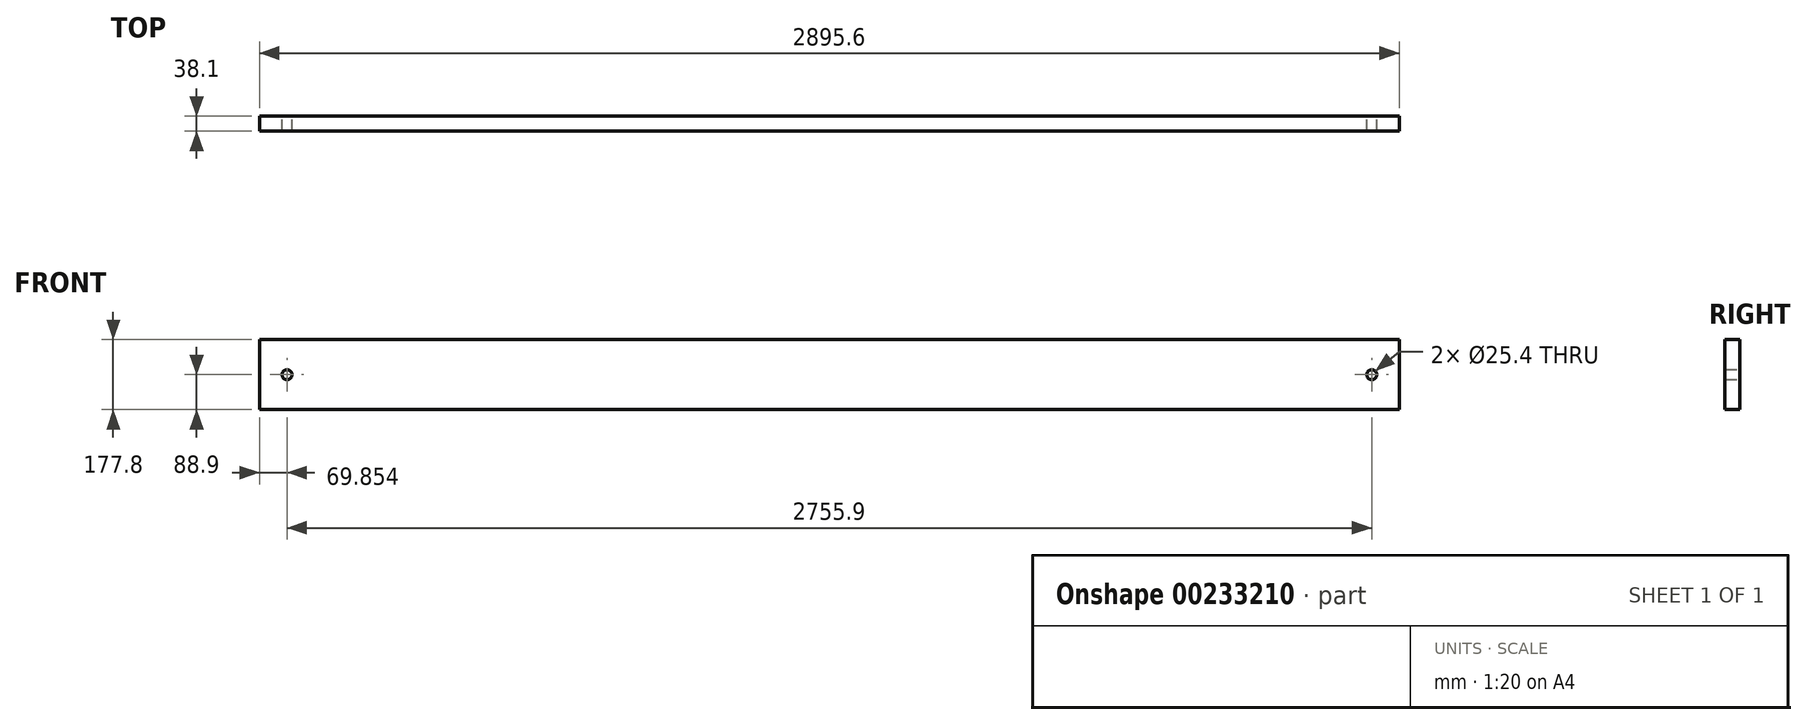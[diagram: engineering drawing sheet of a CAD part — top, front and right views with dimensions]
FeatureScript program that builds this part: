
annotation { "Feature Type Name" : "Feature", "Feature Type Description" : "" }
export const myFeature = defineFeature(function(context is Context, id is Id, definition is map)
    precondition{}
    {
        {
            var Q0;
            Q0=qCreatedBy(makeId("Front.planeOp"),FACE);
            var sketch = newSketch(context, id + "F0", { "sketchPlane" : qUnion([Q0])});
            skLineSegment(sketch, "E0.bottom", {"start": v(-1499.05, -581.52) * mm, "end": v(1396.55, -581.52) * mm});
            skLineSegment(sketch, "E0.top", {"start": v(-1499.05, -759.32) * mm, "end": v(1396.55, -759.32) * mm});
            skLineSegment(sketch, "E0.left", {"start": v(-1499.05, -581.52) * mm, "end": v(-1499.05, -759.32) * mm});
            skLineSegment(sketch, "E0.right", {"start": v(1396.55, -581.52) * mm, "end": v(1396.55, -759.32) * mm});
            skCircle(sketch, "E1", {"center": v(-1429.2, -670.42) * mm, "radius": 12.7 * mm});
            skCircle(sketch, "E2", {"center": v(1326.7, -670.42) * mm, "radius": 12.7 * mm});
            skSolve(sketch);
        }
        {
            var Q0;
            Q0=makeQuery(id+"F0.imprint","IMPRINT",FACE,{"disambiguationData":[TD([[makeQuery(id+"F0.imprint","IMPRINT",EDGE,{"derivedFrom":sQuery(id+"F0.wireOp",EDGE,"E0.bottom")}),-1.0]])]});
            extrude(context, id + "F1", {"entities" : qUnion([Q0]), "depth" : 38.1 * mm});
        }
    });
